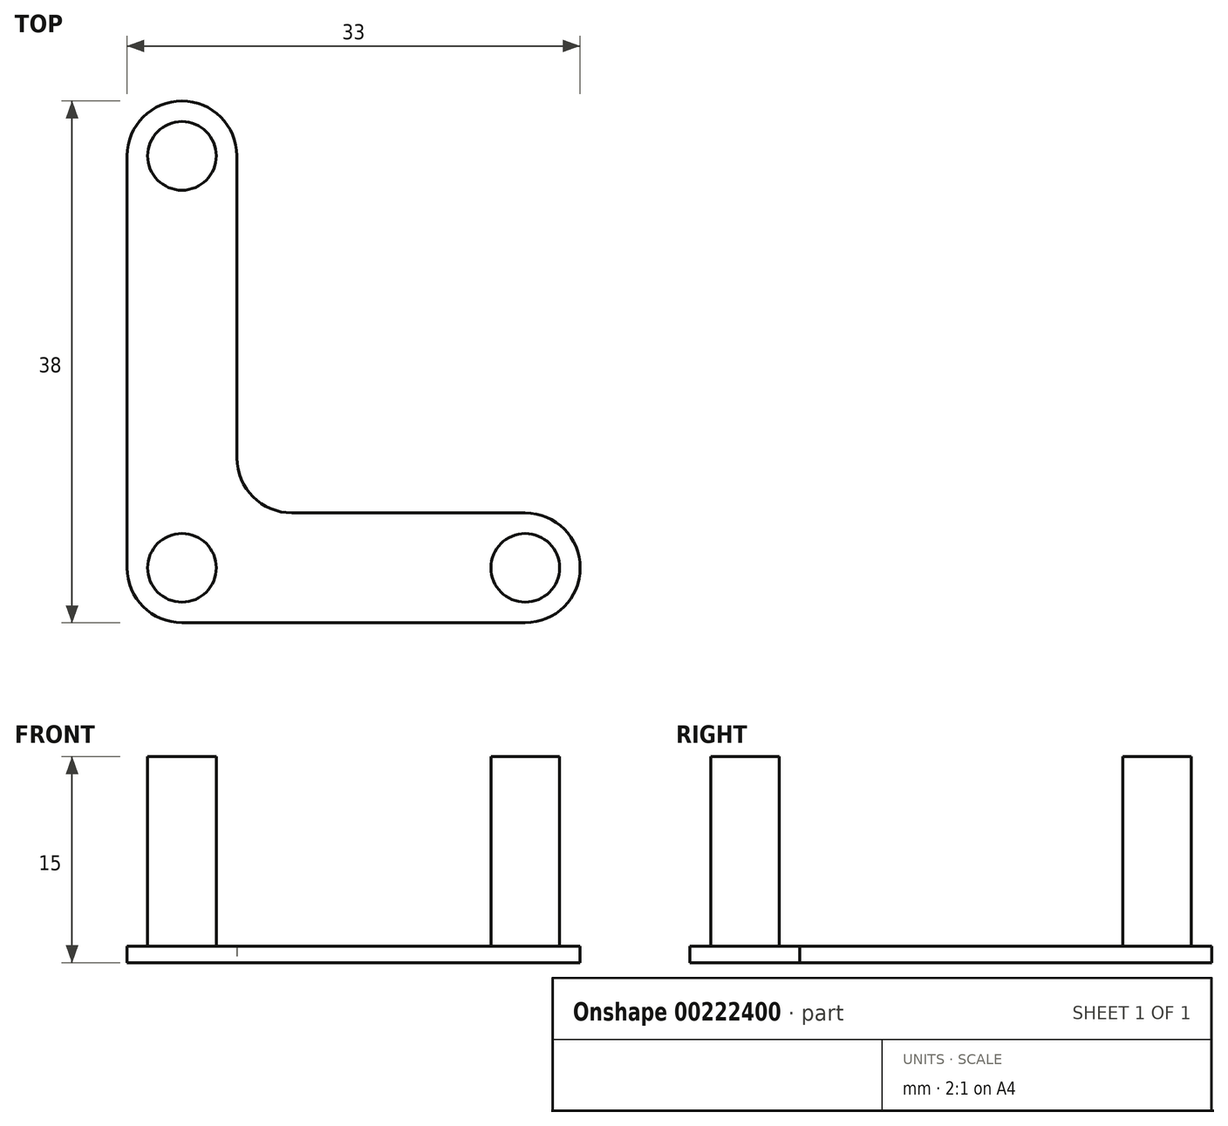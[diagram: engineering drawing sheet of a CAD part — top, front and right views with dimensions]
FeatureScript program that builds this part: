
annotation { "Feature Type Name" : "Feature", "Feature Type Description" : "" }
export const myFeature = defineFeature(function(context is Context, id is Id, definition is map)
    precondition{}
    {
        {
            var Q0;
            Q0=qCreatedBy(makeId("Top.planeOp"),FACE);
            var sketch = newSketch(context, id + "F0", { "sketchPlane" : qUnion([Q0])});
            skCircle(sketch, "E0", {"center": v(0, 0) * mm, "radius": 2.5 * mm});
            skCircle(sketch, "E1", {"center": v(0, 30) * mm, "radius": 2.5 * mm});
            skCircle(sketch, "E2", {"center": v(25, 0) * mm, "radius": 2.5 * mm});
            skLineSegment(sketch, "E3.bottom", {"start": v(-4, 34) * mm, "end": v(4, 34) * mm});
            skLineSegment(sketch, "E3.top", {"start": v(-4, -4) * mm, "end": v(29, -4) * mm});
            skLineSegment(sketch, "E3.left", {"start": v(-4, 34) * mm, "end": v(-4, -4) * mm});
            skLineSegment(sketch, "E3.right", {"start": v(29, 4) * mm, "end": v(29, -4) * mm});
            skLineSegment(sketch, "E4.top", {"start": v(4, 4) * mm, "end": v(29, 4) * mm});
            skLineSegment(sketch, "E4.left", {"start": v(4, 34) * mm, "end": v(4, 4) * mm});
            skLineSegment(sketch, "E5", {"start": v(0, 30) * mm, "end": v(0, 34) * mm, "construction": true});
            skLineSegment(sketch, "E6", {"start": v(25, 0) * mm, "end": v(29, 0) * mm, "construction": true});
            skLineSegment(sketch, "E7", {"start": v(25, 0) * mm, "end": v(25, 4) * mm, "construction": true});
            skSolve(sketch);
        }
        {
            var Q0;
            Q0=makeQuery(id+"F0.imprint","IMPRINT",FACE,{"disambiguationData":[TD([[makeQuery(id+"F0.imprint","IMPRINT",EDGE,{"derivedFrom":sQuery(id+"F0.wireOp",EDGE,"E0")}),-1.0]])]});
            extrude(context, id + "F1", {"entities" : qUnion([Q0]), "depth" : 1.2 * mm, "offsetDistance" : 25 * mm});
        }
        {
            var Q0;
            Q0=makeQuery(id+"F0.imprint","IMPRINT",FACE,{"disambiguationData":[TD([[makeQuery(id+"F0.imprint","IMPRINT",EDGE,{"derivedFrom":sQuery(id+"F0.wireOp",EDGE,"E0")}),1.0]])]});
            var Q1;
            Q1=makeQuery(id+"F0.imprint","IMPRINT",FACE,{"disambiguationData":[TD([[makeQuery(id+"F0.imprint","IMPRINT",EDGE,{"derivedFrom":sQuery(id+"F0.wireOp",EDGE,"E2")}),1.0]])]});
            var Q2;
            Q2=makeQuery(id+"F0.imprint","IMPRINT",FACE,{"disambiguationData":[TD([[makeQuery(id+"F0.imprint","IMPRINT",EDGE,{"derivedFrom":sQuery(id+"F0.wireOp",EDGE,"E1")}),1.0]])]});
            extrude(context, id + "F2", {"entities" : qUnion([Q0, Q1, Q2]), "operationType" : NewBodyOperationType.ADD, "depth" : 15 * mm, "offsetDistance" : 25 * mm});
        }
        {
            var Q0;
            Q0=makeQuery(id+"F1.opExtrude","SWEPT_EDGE",EDGE,{"disambiguationData":[OSD([sQuery(id+"F0.wireOp",EDGE,"E4.top"),sQuery(id+"F0.wireOp",EDGE,"E4.left")])]});
            var Q1;
            Q1=makeQuery(id+"F1.opExtrude","SWEPT_EDGE",EDGE,{"disambiguationData":[OSD([sQuery(id+"F0.wireOp",EDGE,"E3.right"),sQuery(id+"F0.wireOp",EDGE,"E4.top")])]});
            var Q2;
            Q2=makeQuery(id+"F1.opExtrude","SWEPT_EDGE",EDGE,{"disambiguationData":[OSD([sQuery(id+"F0.wireOp",EDGE,"E3.top"),sQuery(id+"F0.wireOp",EDGE,"E3.right")])]});
            var Q3;
            Q3=makeQuery(id+"F1.opExtrude","SWEPT_EDGE",EDGE,{"disambiguationData":[OSD([sQuery(id+"F0.wireOp",EDGE,"E3.top"),sQuery(id+"F0.wireOp",EDGE,"E3.left")])]});
            var Q4;
            Q4=makeQuery(id+"F1.opExtrude","SWEPT_EDGE",EDGE,{"disambiguationData":[OSD([sQuery(id+"F0.wireOp",EDGE,"E3.bottom"),sQuery(id+"F0.wireOp",EDGE,"E3.left")])]});
            var Q5;
            Q5=makeQuery(id+"F1.opExtrude","SWEPT_EDGE",EDGE,{"disambiguationData":[OSD([sQuery(id+"F0.wireOp",EDGE,"E3.bottom"),sQuery(id+"F0.wireOp",EDGE,"E4.left")])]});
            fillet(context, id + "F3", {"entities" : qUnion([Q0, Q1, Q2, Q3, Q4, Q5]), "radius" : 4 * mm, "tangentPropagation" : true, "allowEdgeOverflow" : false});
        }
    });
